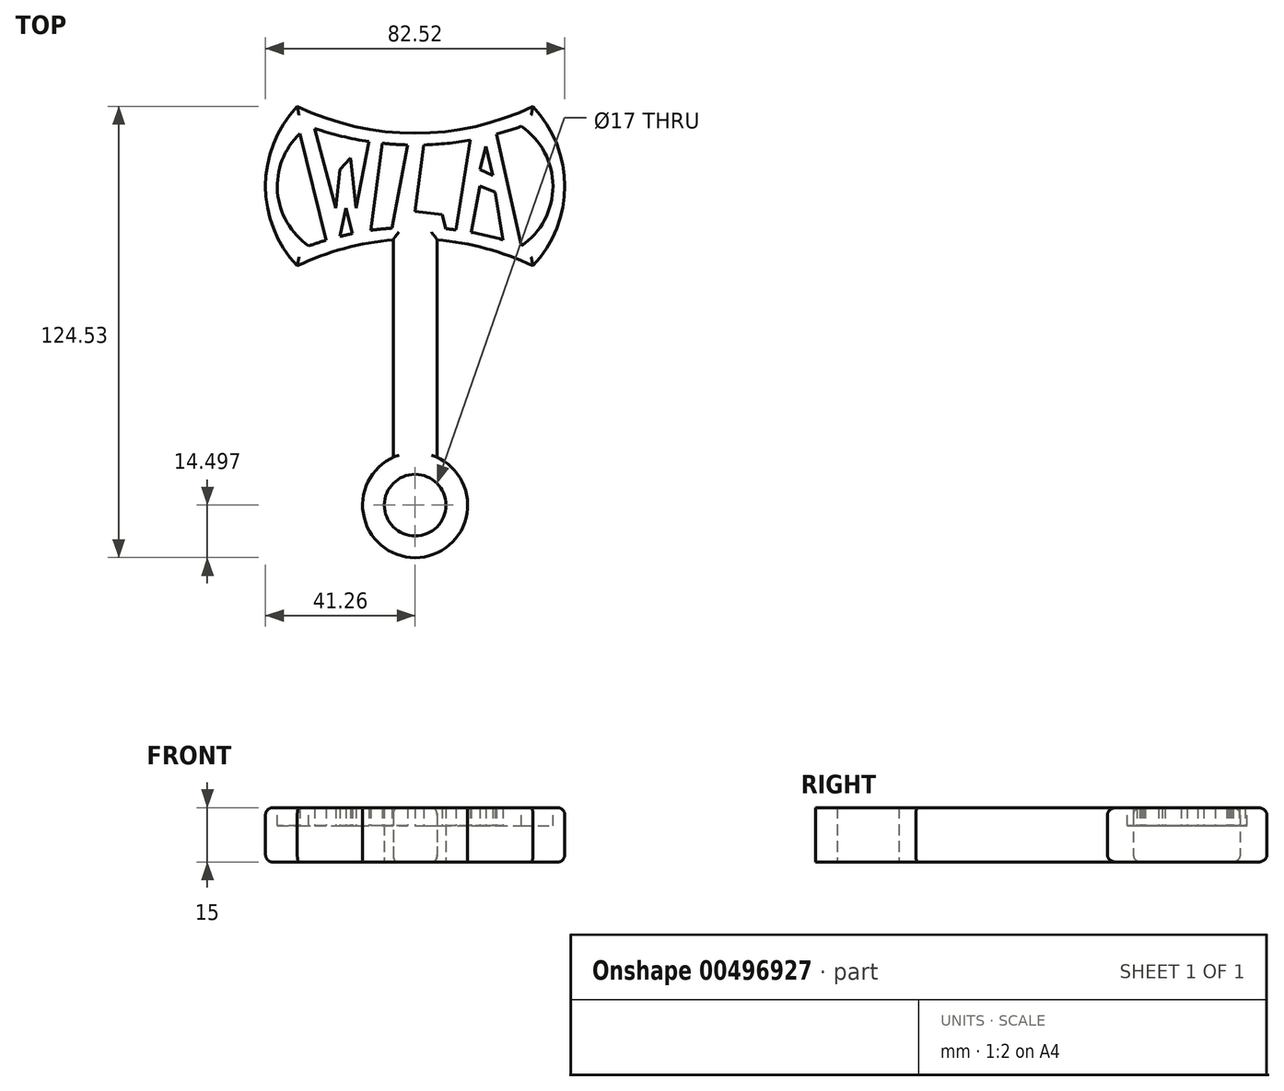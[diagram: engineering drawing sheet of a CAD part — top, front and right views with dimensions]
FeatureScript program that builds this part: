
annotation { "Feature Type Name" : "Feature", "Feature Type Description" : "" }
export const myFeature = defineFeature(function(context is Context, id is Id, definition is map)
    precondition{}
    {
        {
            var Q0;
            Q0=qCreatedBy(makeId("Top.planeOp"),FACE);
            var sketch = newSketch(context, id + "F0", { "sketchPlane" : qUnion([Q0])});
            skArc(sketch, "E0", {"start": v(-32.5, 22) * mm, "mid": v(-41.26, 0) * mm, "end": v(-32.5, -22) * mm});
            skArc(sketch, "E1", {"start": v(-32.5, 22) * mm, "mid": v(0, 14.6) * mm, "end": v(32.5, 22) * mm});
            skArc(sketch, "E2", {"start": v(32.5, -22) * mm, "mid": v(41.26, 0) * mm, "end": v(32.5, 22) * mm});
            skArc(sketch, "E3", {"start": v(32.5, -22) * mm, "mid": v(0, -14.6) * mm, "end": v(-32.5, -22) * mm});
            skLineSegment(sketch, "E4", {"start": v(-32.5, 22) * mm, "end": v(32.5, -22) * mm});
            skLineSegment(sketch, "E5", {"start": v(32.5, 22) * mm, "end": v(-32.5, -22) * mm});
            skLineSegment(sketch, "E6", {"start": v(-32.5, 22) * mm, "end": v(-32.5, -22) * mm});
            skLineSegment(sketch, "E7", {"start": v(32.5, 22) * mm, "end": v(32.5, -22) * mm});
            skLineSegment(sketch, "E8", {"start": v(-6, -14.83) * mm, "end": v(-6, -74.83) * mm});
            skLineSegment(sketch, "E9", {"start": v(-6, -74.83) * mm, "end": v(6, -74.83) * mm});
            skLineSegment(sketch, "E10", {"start": v(6, -74.83) * mm, "end": v(6, -14.83) * mm});
            skArc(sketch, "E11", {"start": v(-6, -74.83) * mm, "mid": v(0, -102.53) * mm, "end": v(6, -74.83) * mm});
            skCircle(sketch, "E12", {"center": v(0, -88.03) * mm, "radius": 8.5 * mm});
            skSolve(sketch);
        }
        {
            var Q0;
            Q0 = qSketchRegion(id + "F0", true);
            extrude(context, id + "F1", {"entities" : qUnion([Q0]), "depth" : 15 * mm});
        }
        {
            var Q0;
            Q0=makeQuery(id+"F1.opExtrude","CAP_EDGE",EDGE,{"disambiguationData":[OSD([sQuery(id+"F0.wireOp",EDGE,"E8")])],"isStart":false});
            var Q1;
            Q1=makeQuery(id+"F1.opExtrude","CAP_EDGE",EDGE,{"disambiguationData":[OSD([sQuery(id+"F0.wireOp",EDGE,"E10")])],"isStart":false});
            var Q2;
            Q2=makeQuery(id+"F1.opExtrude","CAP_EDGE",EDGE,{"disambiguationData":[OSD([sQuery(id+"F0.wireOp",EDGE,"E10")])],"isStart":true});
            var Q3;
            Q3=makeQuery(id+"F1.opExtrude","CAP_EDGE",EDGE,{"disambiguationData":[OSD([sQuery(id+"F0.wireOp",EDGE,"E8")])],"isStart":true});
            fillet(context, id + "F2", {"entities" : qUnion([Q0, Q1, Q2, Q3]), "radius" : 1.5 * mm, "tangentPropagation" : true, "allowEdgeOverflow" : false});
        }
        {
            var Q0;
            Q0=makeQuery(id+"F1.opExtrude","CAP_FACE",FACE,{"disambiguationData":[OSD([sQuery(id+"F0.wireOp",EDGE,"E0"),sQuery(id+"F0.wireOp",EDGE,"E1"),sQuery(id+"F0.wireOp",EDGE,"E2"),sQuery(id+"F0.wireOp",EDGE,"E3"),sQuery(id+"F0.wireOp",EDGE,"E8"),sQuery(id+"F0.wireOp",EDGE,"E10"),sQuery(id+"F0.wireOp",EDGE,"E11"),sQuery(id+"F0.wireOp",EDGE,"E12")])],"isStart":false});
            var sketch = newSketch(context, id + "F3", { "sketchPlane" : qUnion([Q0])});
            skArc(sketch, "E13", {"start": v(-29.31, 16.5) * mm, "mid": v(-38.01, 0) * mm, "end": v(-29.31, -16.5) * mm});
            skArc(sketch, "E14", {"start": v(-29.31, 16.5) * mm, "mid": v(0, 11.34) * mm, "end": v(29.31, 16.5) * mm});
            skArc(sketch, "E15", {"start": v(29.31, -16.5) * mm, "mid": v(38.01, 0) * mm, "end": v(29.31, 16.5) * mm});
            skLineSegment(sketch, "E16", {"start": v(-29.31, 16.5) * mm, "end": v(29.31, -16.5) * mm});
            skLineSegment(sketch, "E17", {"start": v(29.31, 16.5) * mm, "end": v(-29.31, -16.5) * mm});
            skLineSegment(sketch, "E18", {"start": v(-29.31, -16.5) * mm, "end": v(-29.31, 16.5) * mm});
            skLineSegment(sketch, "E19", {"start": v(29.31, 16.5) * mm, "end": v(29.31, -16.5) * mm});
            skLineSegment(sketch, "E20", {"start": v(0, 11.34) * mm, "end": v(0, -13.95) * mm});
            skArc(sketch, "E21", {"start": v(29.31, -16.5) * mm, "mid": v(0, -11.34) * mm, "end": v(-29.31, -16.5) * mm});
            skSolve(sketch);
        }
        {
            var Q0;
            {var subQ0=sQuery(id+"F0.wireOp",EDGE,"E3");Q0=makeQuery(id+"F1.opExtrude","CAP_EDGE",EDGE,{"disambiguationData":[OSD([subQ0]),TDD([makeQuery(id+"F0.imprint","IMPRINT",EDGE,{"disambiguationData":[TD([[makeQuery(id+"F0.imprint","INTERSECT",VERTEX,{"derivedFrom":[subQ0,sQuery(id+"F0.wireOp",EDGE,"E8")]}),-1.0]])],"derivedFrom":subQ0})])],"isStart":false});}
            var Q1;
            Q1=makeQuery(id+"F1.opExtrude","CAP_EDGE",EDGE,{"disambiguationData":[OSD([sQuery(id+"F0.wireOp",EDGE,"E0")])],"isStart":false});
            var Q2;
            {var subQ0=sQuery(id+"F0.wireOp",EDGE,"E3");Q2=makeQuery(id+"F1.opExtrude","CAP_EDGE",EDGE,{"disambiguationData":[OSD([subQ0]),TDD([makeQuery(id+"F0.imprint","IMPRINT",EDGE,{"disambiguationData":[TD([[makeQuery(id+"F0.imprint","INTERSECT",VERTEX,{"derivedFrom":[subQ0,sQuery(id+"F0.wireOp",EDGE,"E10")]}),1.0]])],"derivedFrom":subQ0})])],"isStart":false});}
            var Q3;
            {var subQ0=sQuery(id+"F0.wireOp",EDGE,"E3");Q3=makeQuery(id+"F1.opExtrude","CAP_EDGE",EDGE,{"disambiguationData":[OSD([subQ0]),TDD([makeQuery(id+"F0.imprint","IMPRINT",EDGE,{"disambiguationData":[TD([[makeQuery(id+"F0.imprint","INTERSECT",VERTEX,{"derivedFrom":[subQ0,sQuery(id+"F0.wireOp",EDGE,"E8")]}),-1.0]])],"derivedFrom":subQ0})])],"isStart":true});}
            var Q4;
            Q4=makeQuery(id+"F1.opExtrude","CAP_EDGE",EDGE,{"disambiguationData":[OSD([sQuery(id+"F0.wireOp",EDGE,"E0")])],"isStart":true});
            var Q5;
            Q5=makeQuery(id+"F1.opExtrude","CAP_EDGE",EDGE,{"disambiguationData":[OSD([sQuery(id+"F0.wireOp",EDGE,"E1")])],"isStart":true});
            var Q6;
            Q6=makeQuery(id+"F1.opExtrude","CAP_EDGE",EDGE,{"disambiguationData":[OSD([sQuery(id+"F0.wireOp",EDGE,"E2")])],"isStart":true});
            var Q7;
            {var subQ0=sQuery(id+"F0.wireOp",EDGE,"E3");Q7=makeQuery(id+"F1.opExtrude","CAP_EDGE",EDGE,{"disambiguationData":[OSD([subQ0]),TDD([makeQuery(id+"F0.imprint","IMPRINT",EDGE,{"disambiguationData":[TD([[makeQuery(id+"F0.imprint","INTERSECT",VERTEX,{"derivedFrom":[subQ0,sQuery(id+"F0.wireOp",EDGE,"E10")]}),1.0]])],"derivedFrom":subQ0})])],"isStart":true});}
            var Q8;
            Q8=makeQuery(id+"F1.opExtrude","CAP_EDGE",EDGE,{"disambiguationData":[OSD([sQuery(id+"F0.wireOp",EDGE,"E2")])],"isStart":false});
            var Q9;
            Q9=makeQuery(id+"F1.opExtrude","CAP_EDGE",EDGE,{"disambiguationData":[OSD([sQuery(id+"F0.wireOp",EDGE,"E1")])],"isStart":false});
            fillet(context, id + "F4", {"entities" : qUnion([Q0, Q1, Q2, Q3, Q4, Q5, Q6, Q7, Q8, Q9]), "radius" : 2 * mm, "tangentPropagation" : true, "allowEdgeOverflow" : false});
        }
        {
            var Q0;
            Q0 = qSketchRegion(id + "F3", true);
            extrude(context, id + "F5", {"entities" : qUnion([Q0]), "operationType" : NewBodyOperationType.REMOVE, "oppositeDirection" : true, "depth" : 5 * mm});
        }
        {
            var Q0;
            Q0=makeQuery(id+"F5.boolean.opBoolean","COPY",FACE,{"derivedFrom":makeQuery(id+"F5.opExtrude","CAP_FACE",FACE,{"disambiguationData":[OSD([sQuery(id+"F3.wireOp",EDGE,"E13"),sQuery(id+"F3.wireOp",EDGE,"E14"),sQuery(id+"F3.wireOp",EDGE,"E15"),sQuery(id+"F3.wireOp",EDGE,"E21")])],"isStart":false})});
            var sketch = newSketch(context, id + "F6", { "sketchPlane" : qUnion([Q0])});
            skLineSegment(sketch, "E22", {"start": v(-31.81, 14.48) * mm, "end": v(-24.5, -14.91) * mm});
            skLineSegment(sketch, "E23", {"start": v(-27.76, 15.95) * mm, "end": v(-21.88, -6.07) * mm});
            skLineSegment(sketch, "E24", {"start": v(-21.88, -6.07) * mm, "end": v(-20.68, 4.61) * mm});
            skLineSegment(sketch, "E25", {"start": v(-20.68, 4.61) * mm, "end": v(-17.8, 7.75) * mm});
            skLineSegment(sketch, "E26", {"start": v(-17.8, 7.75) * mm, "end": v(-16.35, -6.07) * mm});
            skLineSegment(sketch, "E27", {"start": v(-16.35, -6.07) * mm, "end": v(-12.69, 12.28) * mm});
            skLineSegment(sketch, "E28", {"start": v(-9.03, 11.82) * mm, "end": v(-12.2, -12.21) * mm});
            skLineSegment(sketch, "E29", {"start": v(-20.68, -13.87) * mm, "end": v(-19.11, -6.07) * mm});
            skLineSegment(sketch, "E30", {"start": v(-19.11, -6.07) * mm, "end": v(-17.24, -13.1) * mm});
            skLineSegment(sketch, "E31", {"start": v(-2.06, 11.37) * mm, "end": v(-6.39, -11.58) * mm});
            skLineSegment(sketch, "E32", {"start": v(0, -6.93) * mm, "end": v(7.4, -7.9) * mm});
            skLineSegment(sketch, "E33", {"start": v(7.4, -7.9) * mm, "end": v(8.43, -11.76) * mm});
            skLineSegment(sketch, "E34", {"start": v(15.2, 12.7) * mm, "end": v(11.33, -12.1) * mm});
            skLineSegment(sketch, "E35", {"start": v(22.44, 14.32) * mm, "end": v(29.31, -16.5) * mm});
            skLineSegment(sketch, "E36", {"start": v(15.45, -12.74) * mm, "end": v(17.82, 0) * mm});
            skLineSegment(sketch, "E37", {"start": v(17.82, 0) * mm, "end": v(22.07, -1.67) * mm});
            skLineSegment(sketch, "E38", {"start": v(22.07, -1.67) * mm, "end": v(24.24, -14.83) * mm});
            skLineSegment(sketch, "E39", {"start": v(19.52, 10.9) * mm, "end": v(17.82, 4.61) * mm});
            skLineSegment(sketch, "E40", {"start": v(17.82, 4.61) * mm, "end": v(21.39, 2.91) * mm});
            skLineSegment(sketch, "E41", {"start": v(21.39, 2.91) * mm, "end": v(19.52, 10.9) * mm});
            skLineSegment(sketch, "E42", {"start": v(0, -6.93) * mm, "end": v(2.41, 11.38) * mm});
            skSolve(sketch);
        }
        {
            var Q0;
            {var subQ4=sQuery(id+"F6.wireOp",EDGE,"E34");Q0=makeQuery(id+"F6.imprint","IMPRINT",FACE,{"disambiguationData":[TD([[makeQuery(id+"F6.imprint","IMPRINT",EDGE,{"derivedFrom":subQ4}),1.0]])]});}
            var Q1;
            {var subQ2=sQuery(id+"F6.wireOp",EDGE,"E31");Q1=makeQuery(id+"F6.imprint","IMPRINT",FACE,{"disambiguationData":[TD([[makeQuery(id+"F6.imprint","IMPRINT",EDGE,{"derivedFrom":subQ2}),1.0]])]});}
            var Q2;
            {var subQ3=sQuery(id+"F6.wireOp",EDGE,"E22");Q2=makeQuery(id+"F6.imprint","IMPRINT",FACE,{"disambiguationData":[TD([[makeQuery(id+"F6.imprint","IMPRINT",EDGE,{"derivedFrom":subQ3}),1.0]])]});}
            extrude(context, id + "F7", {"entities" : qUnion([Q0, Q1, Q2]), "operationType" : NewBodyOperationType.ADD, "depth" : 5 * mm});
        }
    });
